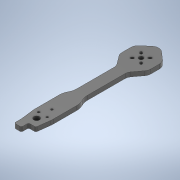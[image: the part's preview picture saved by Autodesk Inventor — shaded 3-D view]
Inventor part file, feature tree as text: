
AUTODESK INVENTOR PART (.ipt)
format: ipt  version: 2020 (Build 240168000, 168)  size: 247,808 bytes
history: native  units: in
note: dims shown in document units (in); Inventor stores cm internally (conversion verified against a paired STEP export)
features: sketch x3, fillet x2, extrude x1, projected_geometry x1
ambient origin geometry x8: Origin, YZ Plane, XZ Plane, XY Plane, X Axis, Y Axis, Z Axis, Center Point
bodies: Solid2 (feature_tree), Solid1 (feature_tree)
feature tree (7):
  sketch  "Sketch1"  dims[d0=7.0in d1=5.72in d2=0.8352in d3=0.2992in]
  sketch  "Sketch2"  dims[d4=0.2992in]
  extrude  "Extrusion1"  Depth=5.72in
  fillet  "Fillet2"  Radius=0.8352in
  fillet  "Fillet3"  Radius=0.2992in
  projected_geometry  "Projected Loop1"
  sketch  "Sketch3"  dims[d5=0.9835in d6=0.9835in d7=0.3937in d8=0.0in d10=0.3937in d11=0.7874in]
